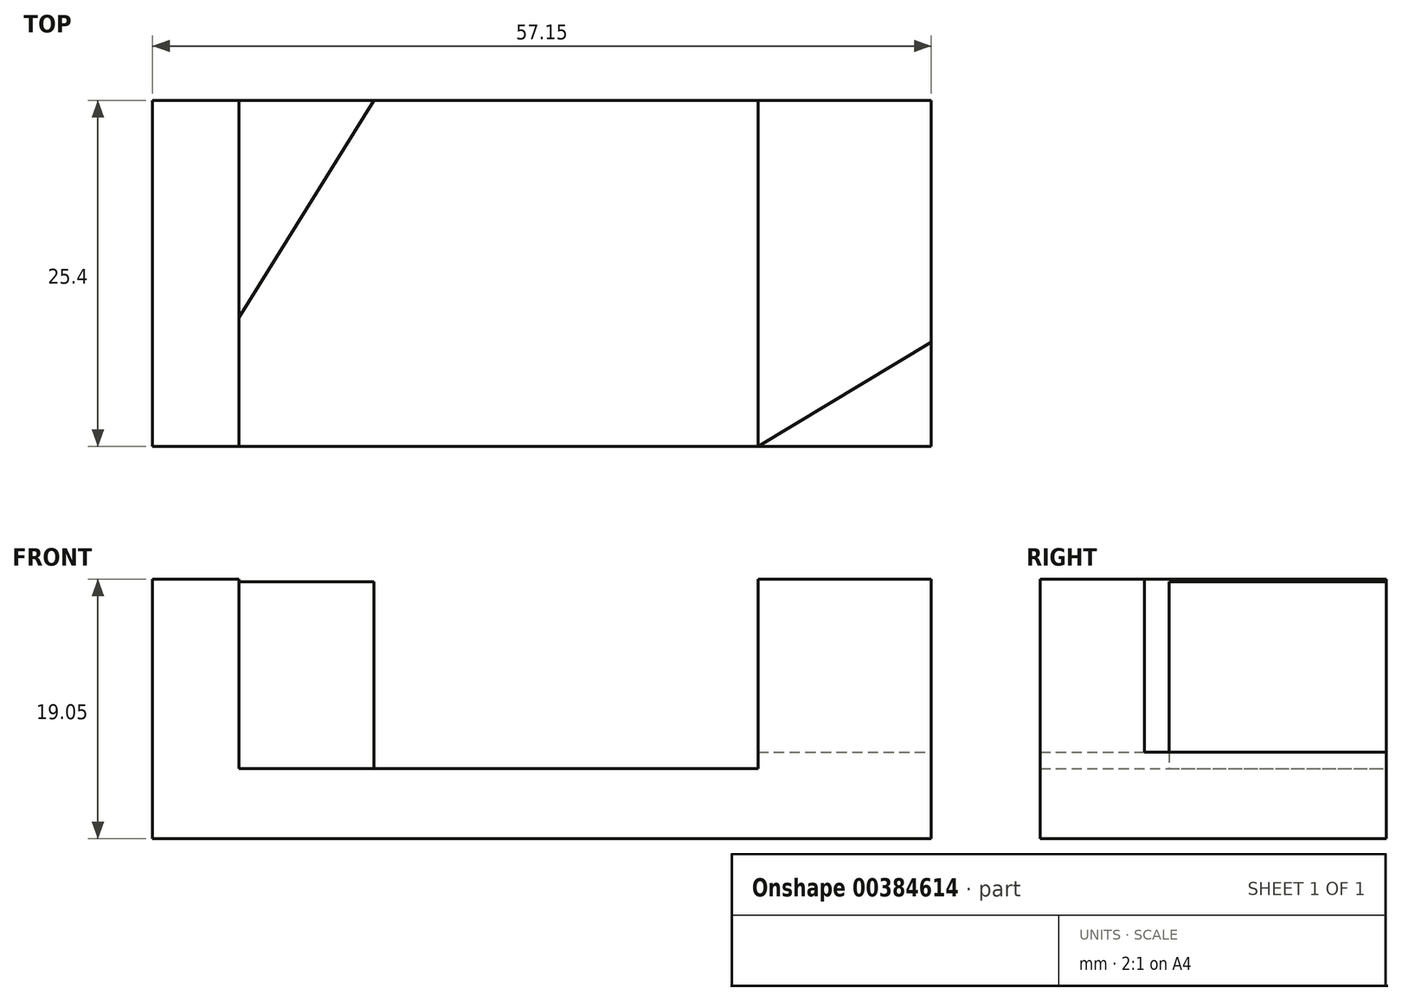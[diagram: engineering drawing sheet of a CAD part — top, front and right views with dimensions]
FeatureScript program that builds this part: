
annotation { "Feature Type Name" : "Feature", "Feature Type Description" : "" }
export const myFeature = defineFeature(function(context is Context, id is Id, definition is map)
    precondition{}
    {
        {
            var Q0;
            Q0=qCreatedBy(makeId("Front.planeOp"),FACE);
            var sketch = newSketch(context, id + "F0", { "sketchPlane" : qUnion([Q0])});
            skLineSegment(sketch, "E0", {"start": v(0, 0) * mm, "end": v(0, 19.05) * mm});
            skLineSegment(sketch, "E1", {"start": v(0, 19.05) * mm, "end": v(6.35, 19.05) * mm});
            skLineSegment(sketch, "E2", {"start": v(6.35, 19.05) * mm, "end": v(6.35, 5.13) * mm});
            skLineSegment(sketch, "E3", {"start": v(44.45, 5.13) * mm, "end": v(44.45, 19.05) * mm});
            skLineSegment(sketch, "E4", {"start": v(44.45, 19.05) * mm, "end": v(57.15, 19.05) * mm});
            skLineSegment(sketch, "E5", {"start": v(57.15, 19.05) * mm, "end": v(57.15, 0) * mm});
            skLineSegment(sketch, "E6", {"start": v(57.15, 0) * mm, "end": v(0, 0) * mm});
            skLineSegment(sketch, "E7", {"start": v(6.35, 5.13) * mm, "end": v(44.45, 5.13) * mm});
            skSolve(sketch);
        }
        {
            var Q0;
            Q0 = qSketchRegion(id + "F0", true);
            extrude(context, id + "F1", {"entities" : qUnion([Q0]), "depth" : 25.4 * mm});
        }
        {
            var Q0;
            Q0=makeQuery(id+"F1.opExtrude","SWEPT_FACE",FACE,{"disambiguationData":[OSD([sQuery(id+"F0.wireOp",EDGE,"E4")])]});
            var sketch = newSketch(context, id + "F2", { "sketchPlane" : qUnion([Q0])});
            skLineSegment(sketch, "E8", {"start": v(44.45, -25.4) * mm, "end": v(57.15, -17.76) * mm});
            skSolve(sketch);
        }
        {
            var Q0;
            {var subQ0=sQuery(id+"F2.wireOp",EDGE,"E8");Q0=makeQuery(id+"F2.imprint","IMPRINT",FACE,{"disambiguationData":[TD([[makeQuery(id+"F2.imprint","IMPRINT",EDGE,{"derivedFrom":subQ0}),1.0]])]});}
            extrude(context, id + "F3", {"entities" : qUnion([Q0]), "operationType" : NewBodyOperationType.REMOVE, "oppositeDirection" : true, "depth" : 12.7 * mm});
        }
        {
            var Q0;
            Q0=makeQuery(id+"F1.opExtrude","SWEPT_FACE",FACE,{"disambiguationData":[OSD([sQuery(id+"F0.wireOp",EDGE,"E7")])]});
            var sketch = newSketch(context, id + "F4", { "sketchPlane" : qUnion([Q0])});
            skLineSegment(sketch, "E9", {"start": v(6.35, -15.94) * mm, "end": v(16.24, 0) * mm});
            skSolve(sketch);
        }
        {
            var Q0;
            {var subQ0=sQuery(id+"F4.wireOp",EDGE,"E9");Q0=makeQuery(id+"F4.imprint","IMPRINT",FACE,{"disambiguationData":[TD([[makeQuery(id+"F4.imprint","IMPRINT",EDGE,{"derivedFrom":subQ0}),1.0]])]});}
            extrude(context, id + "F5", {"entities" : qUnion([Q0]), "operationType" : NewBodyOperationType.ADD, "depth" : 13.72 * mm});
        }
    });
